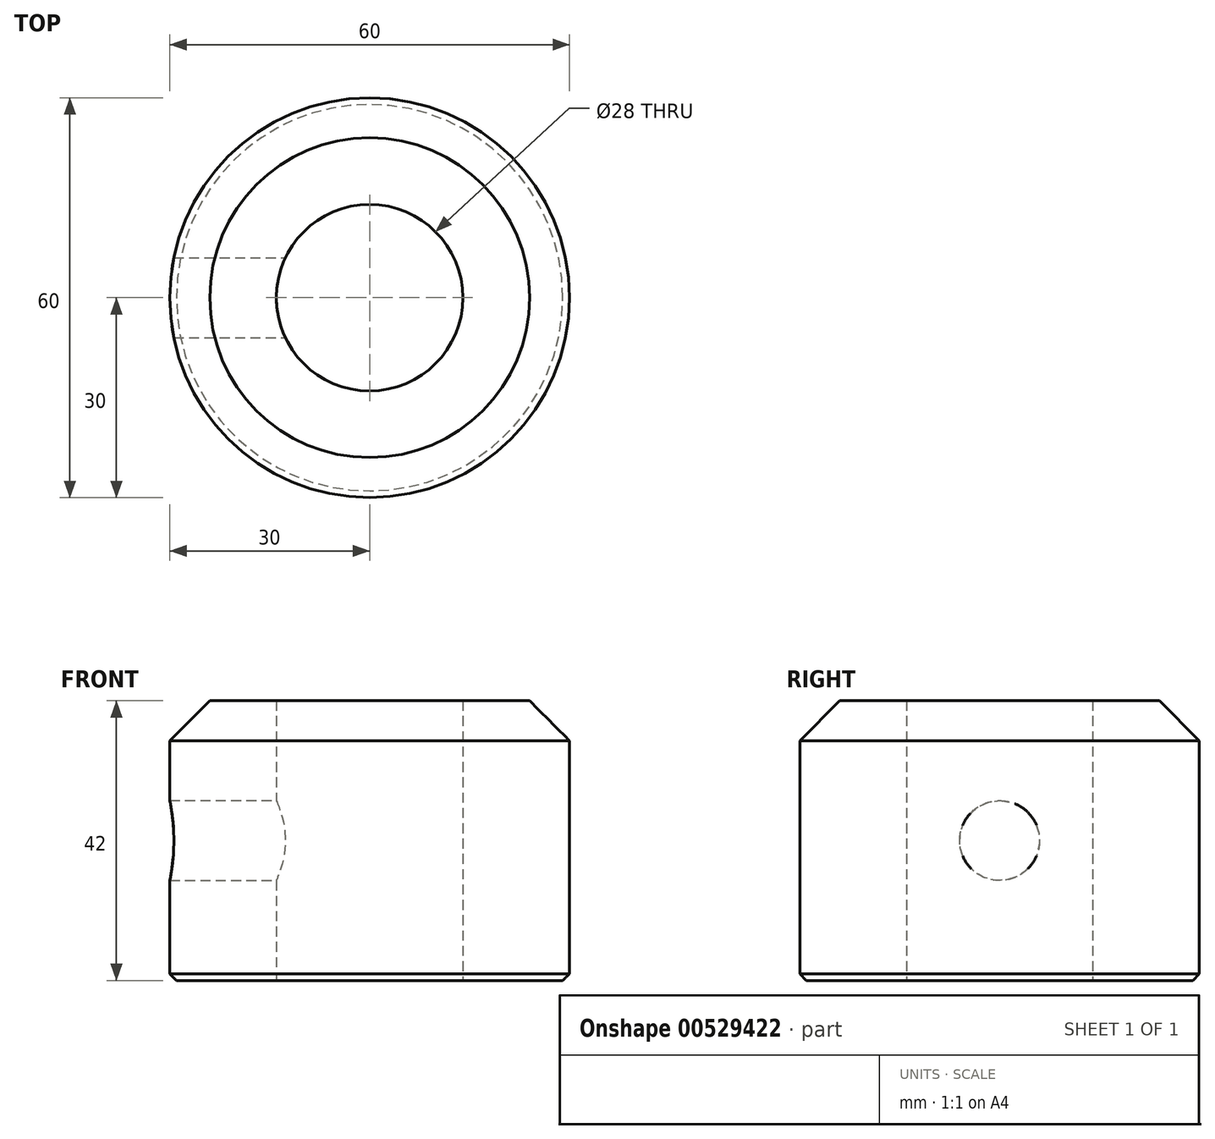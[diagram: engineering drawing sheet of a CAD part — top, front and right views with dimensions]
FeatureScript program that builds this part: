
annotation { "Feature Type Name" : "Feature", "Feature Type Description" : "" }
export const myFeature = defineFeature(function(context is Context, id is Id, definition is map)
    precondition{}
    {
        {
            var Q0;
            Q0=qCreatedBy(makeId("Top.planeOp"),FACE);
            var sketch = newSketch(context, id + "F0", { "sketchPlane" : qUnion([Q0])});
            skCircle(sketch, "E0", {"center": v(0, 0) * mm, "radius": 14 * mm});
            skCircle(sketch, "E1", {"center": v(0, 0) * mm, "radius": 30 * mm});
            skSolve(sketch);
        }
        {
            var Q0;
            Q0=makeQuery(id+"F0.imprint","IMPRINT",FACE,{"disambiguationData":[TD([[makeQuery(id+"F0.imprint","IMPRINT",EDGE,{"derivedFrom":sQuery(id+"F0.wireOp",EDGE,"E0")}),-1.0]])]});
            extrude(context, id + "F1", {"entities" : qUnion([Q0]), "depth" : 42 * mm, "offsetDistance" : 25 * mm});
        }
        {
            var Q0;
            Q0=qCreatedBy(makeId("Right.planeOp"),FACE);
            var sketch = newSketch(context, id + "F2", { "sketchPlane" : qUnion([Q0])});
            skLineSegment(sketch, "E2.0", {"start": v(-30, 42) * mm, "end": v(30, 42) * mm});
            skLineSegment(sketch, "E3", {"start": v(0, 0) * mm, "end": v(0, 21) * mm, "construction": true});
            skPoint(sketch, "E4", {"position": v(0, 21) * mm});
            skLineSegment(sketch, "E5", {"start": v(0, 21) * mm, "end": v(0, 42) * mm, "construction": true});
            skSolve(sketch);
        }
        {
            var Q0;
            Q0=sQuery(id+"F2.wireOp",VERTEX,"E4");
            var Q1;
            Q1=makeQuery(id+"F1.opExtrude","SWEPT_BODY",BODY,{"disambiguationData":[OSD([sQuery(id+"F0.wireOp",EDGE,"E0"),sQuery(id+"F0.wireOp",EDGE,"E1")])]});
            hole(context, id + "F3", {"style" : HoleStyle.SIMPLE, "endStyle" : HoleEndStyle.BLIND, "holeDiameter" : 12 * mm, "holeDepth" : 30 * mm, "isTappedThrough" : true, "tappedDepth" : 12 * mm, "tapClearance" : 3, "locations" : qUnion([Q0]), "scope" : qUnion([Q1])});
        }
        {
            var Q0;
            Q0=makeQuery(id+"F1.opExtrude","CAP_EDGE",EDGE,{"disambiguationData":[OSD([sQuery(id+"F0.wireOp",EDGE,"E1")])],"isStart":false});
            chamfer(context, id + "F4", {"entities" : qUnion([Q0]), "width" : 6 * mm, "tangentPropagation" : true});
        }
        {
            var Q0;
            Q0=makeQuery(id+"F1.opExtrude","CAP_EDGE",EDGE,{"disambiguationData":[OSD([sQuery(id+"F0.wireOp",EDGE,"E1")])],"isStart":true});
            chamfer(context, id + "F5", {"entities" : qUnion([Q0]), "width" : 1 * mm, "tangentPropagation" : true});
        }
    });
